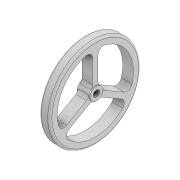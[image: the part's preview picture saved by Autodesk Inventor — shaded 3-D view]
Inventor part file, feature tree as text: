
AUTODESK INVENTOR PART (.ipt)
format: ipt  version: 2022 (Build 260153000, 153)  size: 177,152 bytes
history: native  units: mm
features: extrude x4, sketch x4, fillet x2, projected_geometry x1
ambient origin geometry x8: Origin, YZ Plane, XZ Plane, XY Plane, X Axis, Y Axis, Z Axis, Center Point
bodies: Solid1 (feature_tree)
feature tree (11):
  extrude  "Extrusion1"  Depth=10.0mm TaperAngle=0.0deg
  fillet  "Fillet1"  Radius=2.0mm
  extrude  "Extrusion2"  Depth=12.0mm TaperAngle=0.0deg
  extrude  "Extrusion3"  Depth=3.0mm
  extrude  "Extrusion4"  Depth=5.0mm
  fillet  "Fillet2"  Radius=5.0mm
  sketch  "Sketch1"  dims[d0=85.5mm d1=10.0mm d2=0.0mm d3=2.0mm]
  sketch  "Sketch2"  dims[d9=12.0mm d10=12.0mm d11=0.0mm]
  sketch  "Sketch3"  dims[d12=3.0mm d13=2.5mm]
  sketch  "Sketch4"  dims[d14=0.0mm d15=0.0mm d17=71.5mm d18=5.0mm d19=30.0mm d21=360.0deg d23=0.0mm d24=0.0mm d25=5.0mm]
  projected_geometry  "Project Cut Edges1"
